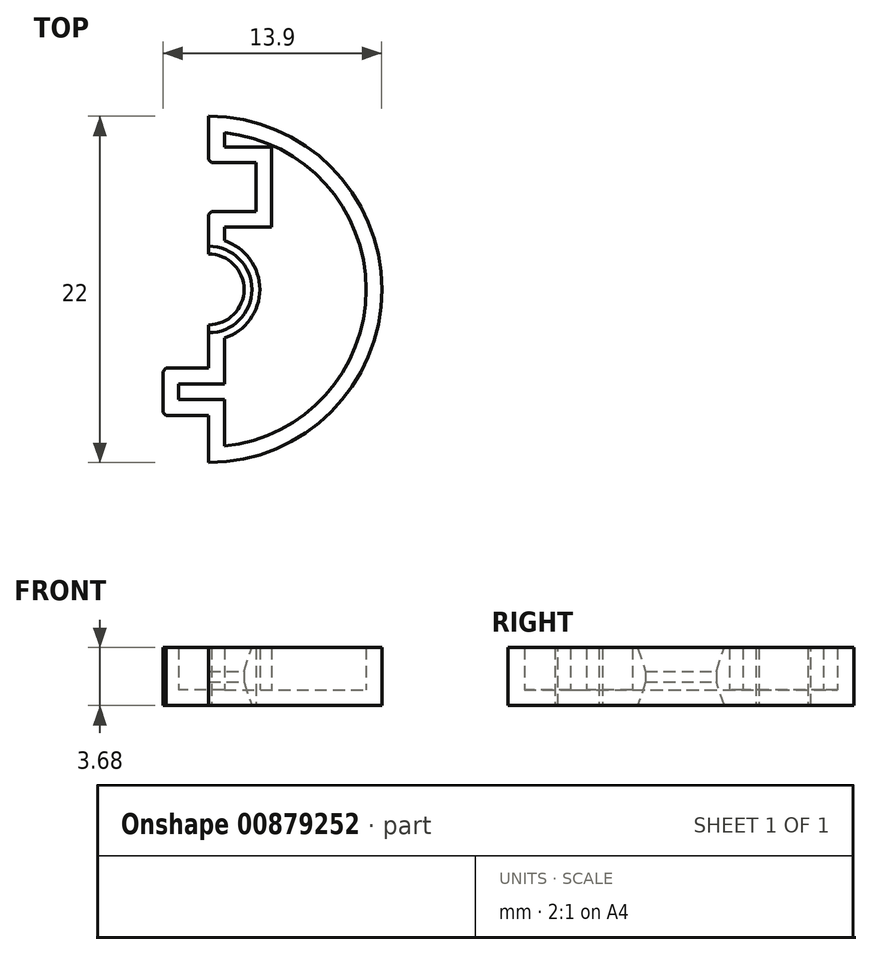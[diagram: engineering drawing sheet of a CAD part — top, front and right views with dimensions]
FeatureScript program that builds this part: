
annotation { "Feature Type Name" : "Feature", "Feature Type Description" : "" }
export const myFeature = defineFeature(function(context is Context, id is Id, definition is map)
    precondition{}
    {
        {
            var Q0;
            Q0=qCreatedBy(makeId("Top.planeOp"),FACE);
            var sketch = newSketch(context, id + "F0", { "sketchPlane" : qUnion([Q0])});
            skArc(sketch, "E0", {"start": v(-22.8, -6.08) * mm, "mid": v(-11.8, 4.92) * mm, "end": v(-22.8, 15.92) * mm});
            skArc(sketch, "E1", {"start": v(-22.8, 2.67) * mm, "mid": v(-20.56, 4.92) * mm, "end": v(-22.8, 7.17) * mm});
            skLineSegment(sketch, "E2", {"start": v(-22.8, 15.92) * mm, "end": v(-22.8, 12.97) * mm});
            skLineSegment(sketch, "E3", {"start": v(-33.8, 4.92) * mm, "end": v(-25.06, 4.92) * mm, "construction": true});
            skLineSegment(sketch, "E4", {"start": v(-22.8, 12.97) * mm, "end": v(-19.8, 12.97) * mm});
            skLineSegment(sketch, "E5", {"start": v(-19.8, 12.97) * mm, "end": v(-19.8, 9.87) * mm});
            skLineSegment(sketch, "E6", {"start": v(-19.8, 9.87) * mm, "end": v(-22.8, 9.87) * mm});
            skLineSegment(sketch, "E7.MirrorCS", {"start": v(-22.8, -3.08) * mm, "end": v(-25.7, -3.08) * mm});
            skLineSegment(sketch, "E8.MirrorCS", {"start": v(-25.7, -0.08) * mm, "end": v(-22.8, -0.08) * mm});
            skLineSegment(sketch, "E9.MirrorCS", {"start": v(-25.7, -3.08) * mm, "end": v(-25.7, -0.08) * mm});
            skLineSegment(sketch, "E10.trimOffspring", {"start": v(-22.8, 9.87) * mm, "end": v(-22.8, 7.17) * mm});
            skLineSegment(sketch, "E11.trimOffspring", {"start": v(-22.8, -3.08) * mm, "end": v(-22.8, -6.08) * mm});
            skLineSegment(sketch, "E12.trimOffspring", {"start": v(-20.56, 4.92) * mm, "end": v(-11.8, 4.92) * mm, "construction": true});
            skLineSegment(sketch, "E13.trimOffspring", {"start": v(-22.8, 2.67) * mm, "end": v(-22.8, -0.08) * mm});
            skLineSegment(sketch, "E14", {"start": v(-22.8, -9.03) * mm, "end": v(-22.8, 19) * mm, "construction": true});
            skSolve(sketch);
        }
        {
            var Q0;
            Q0 = qSketchRegion(id + "F0", true);
            extrude(context, id + "F1", {"entities" : qUnion([Q0]), "depth" : 3.68 * mm, "offsetDistance" : 25 * mm});
        }
        {
            var Q0;
            Q0=makeQuery(id+"F1.opExtrude","CAP_FACE",FACE,{"disambiguationData":[OSD([sQuery(id+"F0.wireOp",EDGE,"E0"),sQuery(id+"F0.wireOp",EDGE,"E1"),sQuery(id+"F0.wireOp",EDGE,"E2"),sQuery(id+"F0.wireOp",EDGE,"E4"),sQuery(id+"F0.wireOp",EDGE,"E5"),sQuery(id+"F0.wireOp",EDGE,"E6"),sQuery(id+"F0.wireOp",EDGE,"E7.MirrorCS"),sQuery(id+"F0.wireOp",EDGE,"E8.MirrorCS"),sQuery(id+"F0.wireOp",EDGE,"E9.MirrorCS"),sQuery(id+"F0.wireOp",EDGE,"E10.trimOffspring"),sQuery(id+"F0.wireOp",EDGE,"E11.trimOffspring"),sQuery(id+"F0.wireOp",EDGE,"E13.trimOffspring")])],"isStart":false});
            shell(context, id + "F2", {"entities" : qUnion([Q0]), "thickness" : 1 * mm});
        }
        {
            var Q0;
            Q0=makeQuery(id+"F1.opExtrude","CAP_EDGE",EDGE,{"disambiguationData":[OSD([sQuery(id+"F0.wireOp",EDGE,"E1")])],"isStart":false});
            var Q1;
            Q1=makeQuery(id+"F1.opExtrude","CAP_EDGE",EDGE,{"disambiguationData":[OSD([sQuery(id+"F0.wireOp",EDGE,"E1")])],"isStart":true});
            chamfer(context, id + "F3", {"entities" : qUnion([Q0, Q1]), "chamferType" : ChamferType.TWO_OFFSETS, "width1" : 1.5 * mm, "oppositeDirection" : false, "width2" : .5 * mm, "tangentPropagation" : true});
        }
        {
            var Q0;
            Q0=makeQuery(id+"F1.opExtrude","SWEPT_EDGE",EDGE,{"disambiguationData":[OSD([sQuery(id+"F0.wireOp",EDGE,"E8.MirrorCS"),sQuery(id+"F0.wireOp",EDGE,"E9.MirrorCS")])]});
            var Q1;
            Q1=makeQuery(id+"F1.opExtrude","SWEPT_EDGE",EDGE,{"disambiguationData":[OSD([sQuery(id+"F0.wireOp",EDGE,"E7.MirrorCS"),sQuery(id+"F0.wireOp",EDGE,"E9.MirrorCS")])]});
            var Q2;
            Q2=makeQuery(id+"F1.opExtrude","SWEPT_EDGE",EDGE,{"disambiguationData":[OSD([sQuery(id+"F0.wireOp",EDGE,"E6"),sQuery(id+"F0.wireOp",EDGE,"E10.trimOffspring")])]});
            var Q3;
            Q3=makeQuery(id+"F1.opExtrude","SWEPT_EDGE",EDGE,{"disambiguationData":[OSD([sQuery(id+"F0.wireOp",EDGE,"E2"),sQuery(id+"F0.wireOp",EDGE,"E4")])]});
            chamfer(context, id + "F4", {"entities" : qUnion([Q0, Q1, Q2, Q3]), "width" : .2 * mm, "tangentPropagation" : true});
        }
    });
